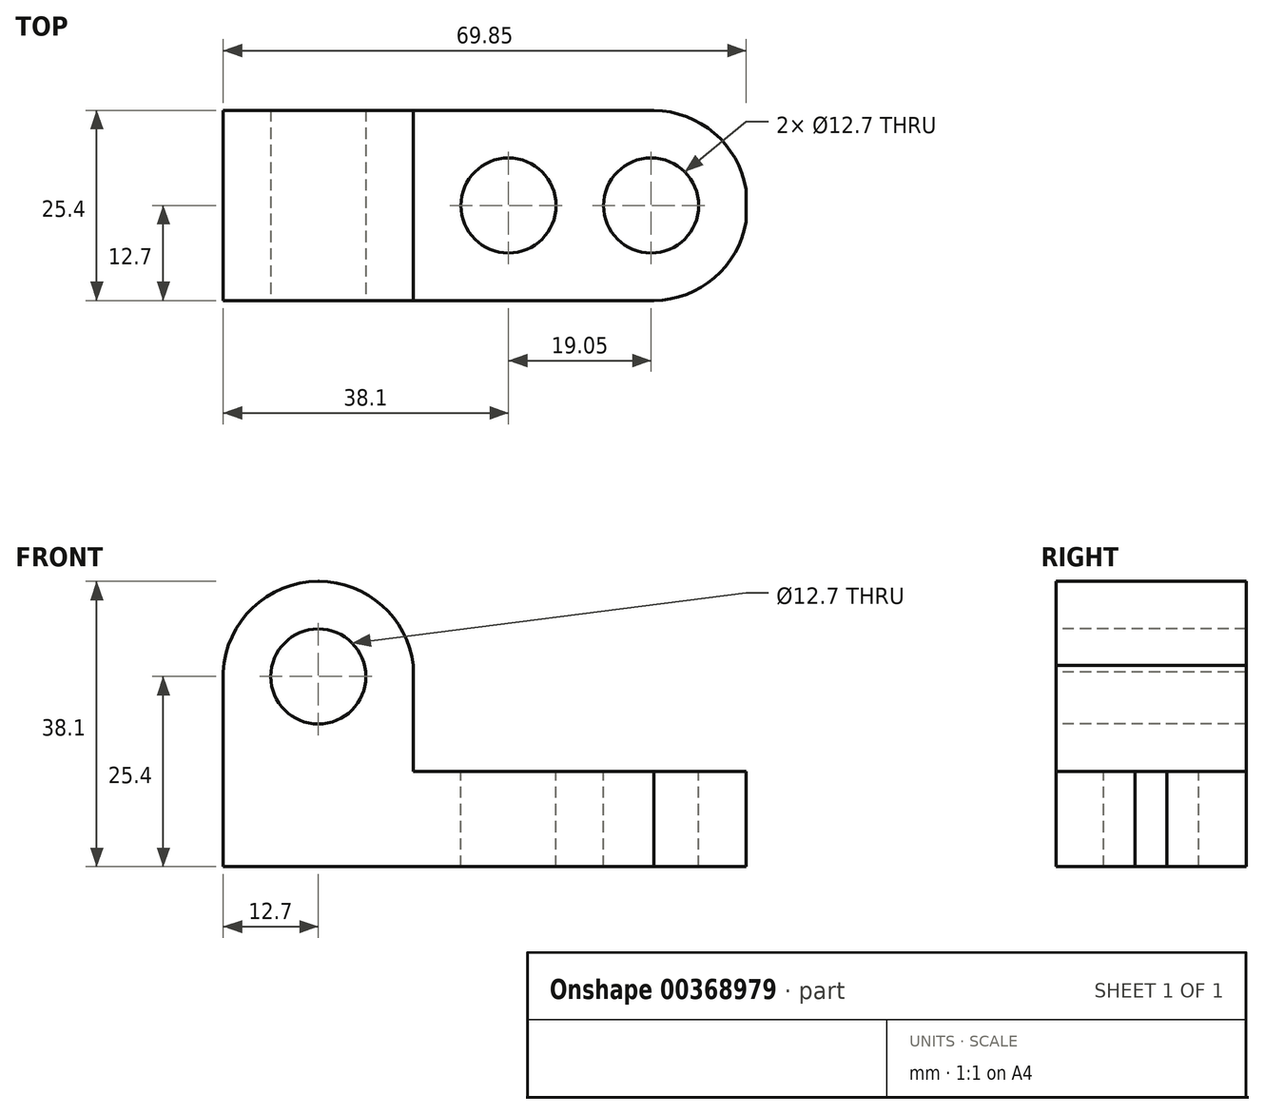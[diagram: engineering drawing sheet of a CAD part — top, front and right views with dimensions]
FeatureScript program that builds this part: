
annotation { "Feature Type Name" : "Feature", "Feature Type Description" : "" }
export const myFeature = defineFeature(function(context is Context, id is Id, definition is map)
    precondition{}
    {
        {
            var Q0;
            Q0=qCreatedBy(makeId("Front.planeOp"),FACE);
            var sketch = newSketch(context, id + "F0", { "sketchPlane" : qUnion([Q0])});
            skLineSegment(sketch, "E0", {"start": v(0, 0) * mm, "end": v(0, 38.1) * mm});
            skLineSegment(sketch, "E1", {"start": v(0, 38.1) * mm, "end": v(25.4, 38.1) * mm});
            skLineSegment(sketch, "E2", {"start": v(25.4, 38.1) * mm, "end": v(25.4, 12.7) * mm});
            skLineSegment(sketch, "E3", {"start": v(25.4, 12.7) * mm, "end": v(69.85, 12.7) * mm});
            skLineSegment(sketch, "E4", {"start": v(69.85, 12.7) * mm, "end": v(69.85, 0) * mm});
            skLineSegment(sketch, "E5", {"start": v(69.85, 0) * mm, "end": v(0, 0) * mm});
            skSolve(sketch);
        }
        {
            var Q0;
            Q0=makeQuery(id+"F0.imprint","IMPRINT",FACE,{"disambiguationData":[TD([[makeQuery(id+"F0.imprint","IMPRINT",EDGE,{"derivedFrom":sQuery(id+"F0.wireOp",EDGE,"E0")}),-1.0]])]});
            extrude(context, id + "F1", {"entities" : qUnion([Q0]), "depth" : 25.4 * mm});
        }
        {
            var Q0;
            Q0=makeQuery(id+"F1.opExtrude","CAP_FACE",FACE,{"disambiguationData":[OSD([sQuery(id+"F0.wireOp",EDGE,"E0"),sQuery(id+"F0.wireOp",EDGE,"E1"),sQuery(id+"F0.wireOp",EDGE,"E2"),sQuery(id+"F0.wireOp",EDGE,"E3"),sQuery(id+"F0.wireOp",EDGE,"E4"),sQuery(id+"F0.wireOp",EDGE,"E5")])],"isStart":false});
            var sketch = newSketch(context, id + "F2", { "sketchPlane" : qUnion([Q0])});
            skCircle(sketch, "E6", {"center": v(12.7, 25.4) * mm, "radius": 6.35 * mm});
            skCircle(sketch, "E7", {"center": v(12.74, 25.35) * mm, "radius": 12.75 * mm});
            skPoint(sketch, "E7.first.point", {"position": v(0, 25.97) * mm});
            skPoint(sketch, "E7.second.point", {"position": v(12.7, 38.1) * mm});
            skPoint(sketch, "E7.third.point", {"position": v(23.63, 31.99) * mm});
            skSolve(sketch);
        }
        {
            var Q0;
            {var subQ0=sQuery(id+"F2.wireOp",EDGE,"E7");var subQ1=makeQuery(id+"F1.opExtrude","CAP_EDGE",EDGE,{"disambiguationData":[OSD([sQuery(id+"F0.wireOp",EDGE,"E1")])],"isStart":false});var subQ2=makeQuery(id+"F2.imprint","INTERSECT",VERTEX,{"disambiguationData":[OD(1.0)],"derivedFrom":[subQ1,subQ0]});var subQ3=makeQuery(id+"F1.opExtrude","CAP_EDGE",EDGE,{"disambiguationData":[OSD([sQuery(id+"F0.wireOp",EDGE,"E0")])],"isStart":false});var subQ4=makeQuery(id+"F2.imprint","INTERSECT",VERTEX,{"disambiguationData":[OD(0.0)],"derivedFrom":[subQ3,subQ0]});Q0=makeQuery(id+"F2.imprint","IMPRINT",FACE,{"disambiguationData":[TD([[makeQuery(id+"F2.imprint","IMPRINT",EDGE,{"disambiguationData":[TD([[subQ2,-1.0],[subQ4,1.0]])],"derivedFrom":subQ0}),-1.0]])]});}
            var Q1;
            {var subQ0=sQuery(id+"F2.wireOp",EDGE,"E7");var subQ1=makeQuery(id+"F1.opExtrude","CAP_EDGE",EDGE,{"disambiguationData":[OSD([sQuery(id+"F0.wireOp",EDGE,"E1")])],"isStart":false});var subQ2=makeQuery(id+"F2.imprint","INTERSECT",VERTEX,{"disambiguationData":[OD(0.0)],"derivedFrom":[subQ1,subQ0]});var subQ3=makeQuery(id+"F1.opExtrude","CAP_EDGE",EDGE,{"disambiguationData":[OSD([sQuery(id+"F0.wireOp",EDGE,"E2")])],"isStart":false});var subQ4=makeQuery(id+"F2.imprint","INTERSECT",VERTEX,{"disambiguationData":[OD(0.0)],"derivedFrom":[subQ3,subQ0]});Q1=makeQuery(id+"F2.imprint","IMPRINT",FACE,{"disambiguationData":[TD([[makeQuery(id+"F2.imprint","IMPRINT",EDGE,{"disambiguationData":[TD([[subQ2,1.0],[subQ4,-1.0]])],"derivedFrom":subQ0}),-1.0]])]});}
            var Q2;
            Q2=makeQuery(id+"F2.imprint","IMPRINT",FACE,{"disambiguationData":[TD([[makeQuery(id+"F2.imprint","IMPRINT",EDGE,{"derivedFrom":sQuery(id+"F2.wireOp",EDGE,"E6")}),1.0]])]});
            extrude(context, id + "F3", {"entities" : qUnion([Q0, Q1, Q2]), "operationType" : NewBodyOperationType.REMOVE, "oppositeDirection" : true, "depth" : 25.4 * mm});
        }
        {
            var Q0;
            Q0=makeQuery(id+"F1.opExtrude","SWEPT_FACE",FACE,{"disambiguationData":[OSD([sQuery(id+"F0.wireOp",EDGE,"E3")])]});
            var sketch = newSketch(context, id + "F4", { "sketchPlane" : qUnion([Q0])});
            skCircle(sketch, "E8", {"center": v(38.1, -12.7) * mm, "radius": 6.35 * mm});
            skCircle(sketch, "E9", {"center": v(57.15, -12.7) * mm, "radius": 6.35 * mm});
            skArc(sketch, "E10", {"start": v(57.15, -25.4) * mm, "mid": v(70.03, -12.7) * mm, "end": v(57.15, 0) * mm});
            skSolve(sketch);
        }
        {
            var Q0;
            Q0=makeQuery(id+"F4.imprint","IMPRINT",FACE,{"disambiguationData":[TD([[makeQuery(id+"F4.imprint","IMPRINT",EDGE,{"derivedFrom":sQuery(id+"F4.wireOp",EDGE,"E8")}),1.0]])]});
            var Q1;
            Q1=makeQuery(id+"F4.imprint","IMPRINT",FACE,{"disambiguationData":[TD([[makeQuery(id+"F4.imprint","IMPRINT",EDGE,{"derivedFrom":sQuery(id+"F4.wireOp",EDGE,"E9")}),1.0]])]});
            var Q2;
            {var subQ0=sQuery(id+"F4.wireOp",EDGE,"E10");var subQ1=sQuery(id+"F0.wireOp",EDGE,"E3");var subQ4=makeQuery(id+"F1.opExtrude","CAP_EDGE",EDGE,{"disambiguationData":[OSD([subQ1])],"isStart":true});var subQ5=makeQuery(id+"F4.imprint","INTERSECT",VERTEX,{"disambiguationData":[OD(1.0)],"derivedFrom":[subQ4,subQ0]});Q2=makeQuery(id+"F4.imprint","IMPRINT",FACE,{"disambiguationData":[TD([[makeQuery(id+"F4.imprint","IMPRINT",EDGE,{"disambiguationData":[TD([[subQ5,1.0]])],"derivedFrom":subQ0}),-1.0]])]});}
            var Q3;
            {var subQ0=sQuery(id+"F4.wireOp",EDGE,"E10");var subQ1=sQuery(id+"F0.wireOp",EDGE,"E3");var subQ2=makeQuery(id+"F1.opExtrude","CAP_EDGE",EDGE,{"disambiguationData":[OSD([subQ1])],"isStart":false});var subQ3=makeQuery(id+"F4.imprint","INTERSECT",VERTEX,{"disambiguationData":[OD(1.0)],"derivedFrom":[subQ2,subQ0]});Q3=makeQuery(id+"F4.imprint","IMPRINT",FACE,{"disambiguationData":[TD([[makeQuery(id+"F4.imprint","IMPRINT",EDGE,{"disambiguationData":[TD([[subQ3,-1.0]])],"derivedFrom":subQ0}),-1.0]])]});}
            extrude(context, id + "F5", {"entities" : qUnion([Q0, Q1, Q2, Q3]), "operationType" : NewBodyOperationType.REMOVE, "oppositeDirection" : true, "depth" : 12.7 * mm});
        }
    });
